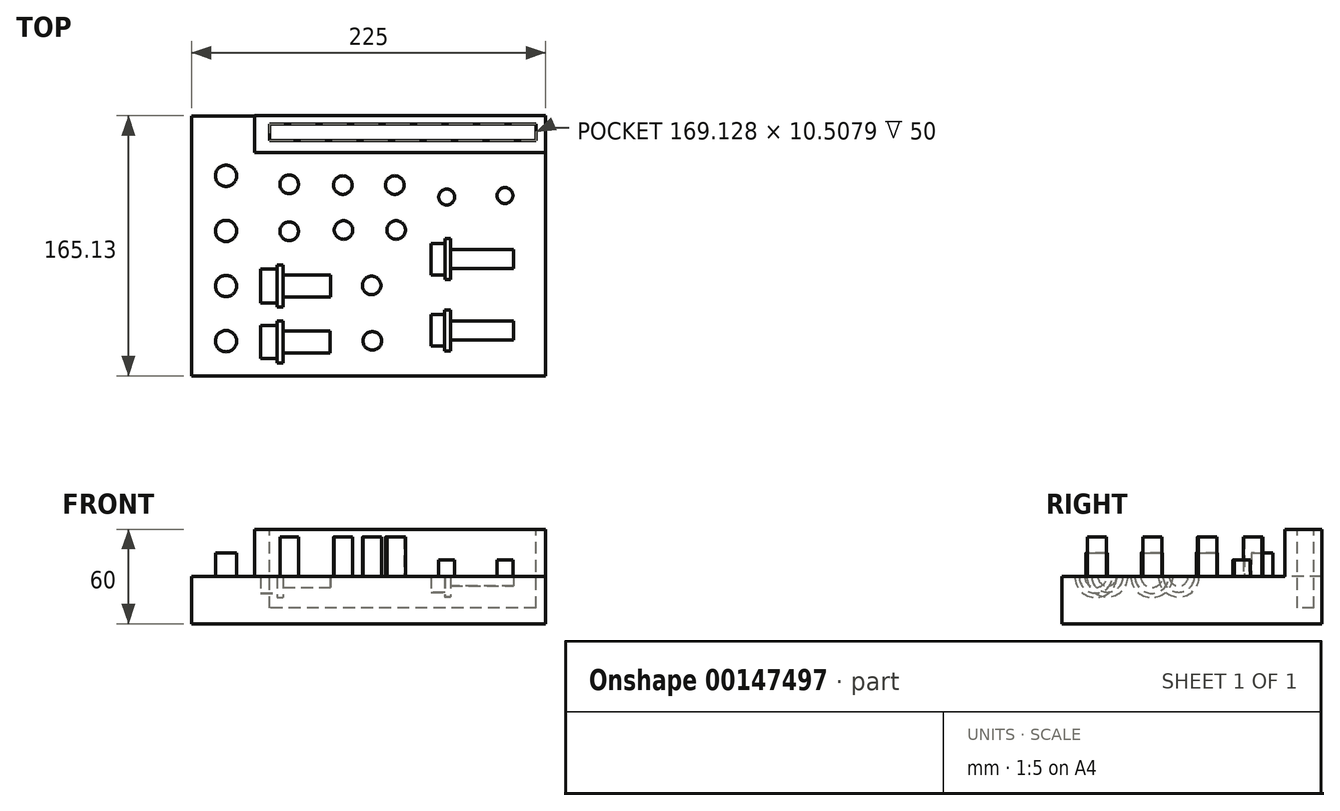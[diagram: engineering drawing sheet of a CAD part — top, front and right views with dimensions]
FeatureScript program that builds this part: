
annotation { "Feature Type Name" : "Feature", "Feature Type Description" : "" }
export const myFeature = defineFeature(function(context is Context, id is Id, definition is map)
    precondition{}
    {
        {
            var Q0;
            Q0=qCreatedBy(makeId("Top.planeOp"),FACE);
            var sketch = newSketch(context, id + "F0", { "sketchPlane" : qUnion([Q0])});
            skLineSegment(sketch, "E0.bottom", {"start": v(0, 0) * mm, "end": v(225, 0) * mm});
            skLineSegment(sketch, "E0.top", {"start": v(0, 165) * mm, "end": v(225, 165) * mm});
            skLineSegment(sketch, "E0.left", {"start": v(0, 0) * mm, "end": v(0, 165) * mm});
            skLineSegment(sketch, "E0.right", {"start": v(225, 0) * mm, "end": v(225, 165) * mm});
            skSolve(sketch);
        }
        {
            var Q0;
            Q0=makeQuery(id+"F0.imprint","IMPRINT",FACE,{"disambiguationData":[TD([[makeQuery(id+"F0.imprint","IMPRINT",EDGE,{"derivedFrom":sQuery(id+"F0.wireOp",EDGE,"E0.bottom")}),1.0]])]});
            extrude(context, id + "F1", {"entities" : qUnion([Q0]), "depth" : 30 * mm});
        }
        {
            var Q0;
            Q0=makeQuery(id+"F1.opExtrude","CAP_FACE",FACE,{"disambiguationData":[OSD([sQuery(id+"F0.wireOp",EDGE,"E0.bottom"),sQuery(id+"F0.wireOp",EDGE,"E0.top"),sQuery(id+"F0.wireOp",EDGE,"E0.left"),sQuery(id+"F0.wireOp",EDGE,"E0.right")])],"isStart":false});
            var sketch = newSketch(context, id + "F2", { "sketchPlane" : qUnion([Q0])});
            skLineSegment(sketch, "E1", {"start": v(0, 0) * mm, "end": v(22, 0) * mm, "construction": true});
            skLineSegment(sketch, "E2", {"start": v(22, 0) * mm, "end": v(22, 22) * mm, "construction": true});
            skLineSegment(sketch, "E3", {"start": v(22, 22) * mm, "end": v(22, 57) * mm, "construction": true});
            skLineSegment(sketch, "E4", {"start": v(22, 57) * mm, "end": v(22, 92) * mm, "construction": true});
            skLineSegment(sketch, "E5", {"start": v(22, 92) * mm, "end": v(22, 127) * mm, "construction": true});
            skCircle(sketch, "E6", {"center": v(22, 127) * mm, "radius": 6.75 * mm});
            skCircle(sketch, "E7", {"center": v(22, 92) * mm, "radius": 6.75 * mm});
            skCircle(sketch, "E8", {"center": v(22, 57) * mm, "radius": 6.75 * mm});
            skCircle(sketch, "E9", {"center": v(22, 22) * mm, "radius": 6.75 * mm});
            skSolve(sketch);
        }
        {
            var Q0;
            Q0=makeQuery(id+"F2.imprint","IMPRINT",FACE,{"disambiguationData":[TD([[makeQuery(id+"F2.imprint","IMPRINT",EDGE,{"derivedFrom":sQuery(id+"F2.wireOp",EDGE,"E6")}),1.0]])]});
            var Q1;
            Q1=makeQuery(id+"F2.imprint","IMPRINT",FACE,{"disambiguationData":[TD([[makeQuery(id+"F2.imprint","IMPRINT",EDGE,{"derivedFrom":sQuery(id+"F2.wireOp",EDGE,"E7")}),1.0]])]});
            var Q2;
            Q2=makeQuery(id+"F2.imprint","IMPRINT",FACE,{"disambiguationData":[TD([[makeQuery(id+"F2.imprint","IMPRINT",EDGE,{"derivedFrom":sQuery(id+"F2.wireOp",EDGE,"E8")}),1.0]])]});
            var Q3;
            Q3=makeQuery(id+"F2.imprint","IMPRINT",FACE,{"disambiguationData":[TD([[makeQuery(id+"F2.imprint","IMPRINT",EDGE,{"derivedFrom":sQuery(id+"F2.wireOp",EDGE,"E9")}),1.0]])]});
            extrude(context, id + "F3", {"entities" : qUnion([Q0, Q1, Q2, Q3]), "operationType" : NewBodyOperationType.ADD, "depth" : 15 * mm});
        }
        {
            var Q0;
            Q0=makeQuery(id+"F1.opExtrude","CAP_FACE",FACE,{"disambiguationData":[OSD([sQuery(id+"F0.wireOp",EDGE,"E0.bottom"),sQuery(id+"F0.wireOp",EDGE,"E0.top"),sQuery(id+"F0.wireOp",EDGE,"E0.left"),sQuery(id+"F0.wireOp",EDGE,"E0.right")])],"isStart":false});
            var sketch = newSketch(context, id + "F4", { "sketchPlane" : qUnion([Q0])});
            skLineSegment(sketch, "E10", {"start": v(0, 0) * mm, "end": v(44, 0) * mm});
            skLineSegment(sketch, "E11", {"start": v(44, 0) * mm, "end": v(44, 22) * mm});
            skLineSegment(sketch, "E12", {"start": v(44, 22) * mm, "end": v(44, 57) * mm});
            skLineSegment(sketch, "E13.bottom", {"start": v(44, 57) * mm, "end": v(54.5, 57) * mm});
            skLineSegment(sketch, "E13.top", {"start": v(44, 46.25) * mm, "end": v(54.5, 46.25) * mm});
            skLineSegment(sketch, "E13.left", {"start": v(44, 57) * mm, "end": v(44, 46.25) * mm});
            skLineSegment(sketch, "E14.bottom", {"start": v(54.5, 57) * mm, "end": v(58.25, 57) * mm});
            skLineSegment(sketch, "E14.top", {"start": v(54.5, 43.65) * mm, "end": v(58.25, 43.65) * mm});
            skLineSegment(sketch, "E14.left", {"start": v(54.5, 46.25) * mm, "end": v(54.5, 43.65) * mm});
            skLineSegment(sketch, "E14.right", {"start": v(58.25, 50) * mm, "end": v(58.25, 43.65) * mm});
            skLineSegment(sketch, "E15.bottom", {"start": v(58.25, 57) * mm, "end": v(88.25, 57) * mm});
            skLineSegment(sketch, "E15.top", {"start": v(58.25, 50) * mm, "end": v(88.25, 50) * mm});
            skLineSegment(sketch, "E15.right", {"start": v(88.25, 57) * mm, "end": v(88.25, 50) * mm});
            skSolve(sketch);
        }
        {
            var Q0;
            {var subQ2=sQuery(id+"F4.wireOp",EDGE,"E10");Q0=makeQuery(id+"F4.imprint","IMPRINT",FACE,{"disambiguationData":[TD([[makeQuery(id+"F4.imprint","IMPRINT",EDGE,{"derivedFrom":subQ2}),1.0]])]});}
            var sketch = newSketch(context, id + "F5", { "sketchPlane" : qUnion([Q0])});
            skLineSegment(sketch, "E16.bottom", {"start": v(43.99, 21.41) * mm, "end": v(54.49, 21.41) * mm});
            skLineSegment(sketch, "E16.top", {"start": v(43.99, 10.87) * mm, "end": v(54.49, 10.87) * mm});
            skLineSegment(sketch, "E16.left", {"start": v(43.99, 21.41) * mm, "end": v(43.99, 10.87) * mm});
            skLineSegment(sketch, "E16.right", {"start": v(54.49, 21.41) * mm, "end": v(54.49, 10.87) * mm});
            skLineSegment(sketch, "E17.bottom", {"start": v(54.49, 21.41) * mm, "end": v(58.24, 21.41) * mm});
            skLineSegment(sketch, "E17.top", {"start": v(54.49, 8.06) * mm, "end": v(58.24, 8.06) * mm});
            skLineSegment(sketch, "E17.left", {"start": v(54.49, 21.41) * mm, "end": v(54.49, 8.06) * mm});
            skLineSegment(sketch, "E17.right", {"start": v(58.24, 21.41) * mm, "end": v(58.24, 8.06) * mm});
            skLineSegment(sketch, "E18.bottom", {"start": v(58.24, 21.41) * mm, "end": v(88.24, 21.41) * mm});
            skLineSegment(sketch, "E18.top", {"start": v(58.24, 14.41) * mm, "end": v(88.24, 14.41) * mm});
            skLineSegment(sketch, "E18.left", {"start": v(58.24, 21.41) * mm, "end": v(58.24, 14.41) * mm});
            skLineSegment(sketch, "E18.right", {"start": v(88.24, 21.41) * mm, "end": v(88.24, 14.41) * mm});
            skSolve(sketch);
        }
        {
            var Q0;
            {var subQ0=sQuery(id+"F5.wireOp",EDGE,"E16.bottom");Q0=makeQuery(id+"F5.imprint","IMPRINT",FACE,{"disambiguationData":[TD([[makeQuery(id+"F5.imprint","IMPRINT",EDGE,{"derivedFrom":subQ0}),-1.0]])]});}
            var Q1;
            {var subQ3=sQuery(id+"F5.wireOp",EDGE,"E17.bottom");Q1=makeQuery(id+"F5.imprint","IMPRINT",FACE,{"disambiguationData":[TD([[makeQuery(id+"F5.imprint","IMPRINT",EDGE,{"derivedFrom":subQ3}),-1.0]])]});}
            var Q2;
            Q2=makeQuery(id+"F5.imprint","IMPRINT",FACE,{"disambiguationData":[TD([[makeQuery(id+"F5.imprint","IMPRINT",EDGE,{"derivedFrom":sQuery(id+"F5.wireOp",EDGE,"E18.bottom")}),-1.0]])]});
            var Q3;
            Q3=sQuery(id+"F5.wireOp",EDGE,"E16.bottom");
            revolve(context, id + "F6", {"operationType" : NewBodyOperationType.REMOVE, "entities" : qUnion([Q0, Q1, Q2]), "axis" : qUnion([Q3]), "revolveType" : RevolveType.FULL, "oppositeDirection" : true});
        }
        {
            var Q0;
            {var subQ2=sQuery(id+"F4.wireOp",EDGE,"E10");Q0=makeQuery(id+"F4.imprint","IMPRINT",FACE,{"disambiguationData":[TD([[makeQuery(id+"F4.imprint","IMPRINT",EDGE,{"derivedFrom":subQ2}),1.0]])]});}
            var sketch = newSketch(context, id + "F7", { "sketchPlane" : qUnion([Q0])});
            skSolve(sketch);
        }
        {
            var Q0;
            Q0=makeQuery(id+"F7.imprint","IMPRINT",FACE,{"disambiguationData":[TD([[makeQuery(id+"F7.imprint","IMPRINT",EDGE,{"derivedFrom":makeQuery(id+"F4.imprint","IMPRINT",EDGE,{"derivedFrom":sQuery(id+"F4.wireOp",EDGE,"E13.bottom")})}),-1.0]])]});
            var Q1;
            Q1=sQuery(id+"F4.wireOp",EDGE,"E13.bottom");
            revolve(context, id + "F8", {"operationType" : NewBodyOperationType.REMOVE, "entities" : qUnion([Q0]), "axis" : qUnion([Q1]), "revolveType" : RevolveType.FULL, "oppositeDirection" : true});
        }
        {
            var Q0;
            Q0=makeQuery(id+"F1.opExtrude","CAP_FACE",FACE,{"disambiguationData":[OSD([sQuery(id+"F0.wireOp",EDGE,"E0.bottom"),sQuery(id+"F0.wireOp",EDGE,"E0.top"),sQuery(id+"F0.wireOp",EDGE,"E0.left"),sQuery(id+"F0.wireOp",EDGE,"E0.right")])],"isStart":false});
            var sketch = newSketch(context, id + "F9", { "sketchPlane" : qUnion([Q0])});
            skLineSegment(sketch, "E19.bottom", {"start": v(0, 0) * mm, "end": v(109.82, 0) * mm, "construction": true});
            skLineSegment(sketch, "E19.top", {"start": v(0, 27.52) * mm, "end": v(109.82, 27.52) * mm, "construction": true});
            skLineSegment(sketch, "E19.left", {"start": v(0, 0) * mm, "end": v(0, 27.52) * mm, "construction": true});
            skLineSegment(sketch, "E19.right", {"start": v(109.82, 0) * mm, "end": v(109.82, 27.52) * mm, "construction": true});
            skSolve(sketch);
        }
        {
            var Q0;
            {var subQ3=sQuery(id+"F0.wireOp",EDGE,"E0.bottom");Q0=makeQuery(id+"F9.imprint","IMPRINT",FACE,{"disambiguationData":[TD([[makeQuery(id+"F9.imprint","IMPRINT",EDGE,{"derivedFrom":makeQuery(id+"F1.opExtrude","CAP_EDGE",EDGE,{"disambiguationData":[OSD([subQ3])],"isStart":false})}),1.0]])]});}
            var sketch = newSketch(context, id + "F10", { "sketchPlane" : qUnion([Q0])});
            skLineSegment(sketch, "E20.bottom", {"start": v(0, 0) * mm, "end": v(62.12, 0) * mm, "construction": true});
            skLineSegment(sketch, "E20.top", {"start": v(0, 121.58) * mm, "end": v(62.12, 121.58) * mm, "construction": true});
            skLineSegment(sketch, "E20.left", {"start": v(0, 0) * mm, "end": v(0, 121.58) * mm, "construction": true});
            skLineSegment(sketch, "E20.right", {"start": v(62.12, 0) * mm, "end": v(62.12, 121.58) * mm, "construction": true});
            skCircle(sketch, "E21", {"center": v(62.12, 121.58) * mm, "radius": 5.9 * mm});
            skCircle(sketch, "E22", {"center": v(62.12, 91.76) * mm, "radius": 5.9 * mm});
            skCircle(sketch, "E23", {"center": v(96.63, 92.6) * mm, "radius": 5.9 * mm});
            skCircle(sketch, "E24", {"center": v(96.19, 121.12) * mm, "radius": 5.9 * mm});
            skCircle(sketch, "E25", {"center": v(114.9, 22.16) * mm, "radius": 5.9 * mm});
            skCircle(sketch, "E26", {"center": v(129.18, 121.12) * mm, "radius": 5.9 * mm});
            skCircle(sketch, "E27", {"center": v(130.07, 92.6) * mm, "radius": 5.9 * mm});
            skCircle(sketch, "E28", {"center": v(114.46, 57.37) * mm, "radius": 5.9 * mm});
            skSolve(sketch);
        }
        {
            var Q0;
            Q0=makeQuery(id+"F10.imprint","IMPRINT",FACE,{"disambiguationData":[TD([[makeQuery(id+"F10.imprint","IMPRINT",EDGE,{"derivedFrom":sQuery(id+"F10.wireOp",EDGE,"CW1vxD1U-gibG-Lz99-enL3-3w2vIjQjNwkh")}),1.0]])]});
            var Q1;
            Q1=makeQuery(id+"F10.imprint","IMPRINT",FACE,{"disambiguationData":[TD([[makeQuery(id+"F10.imprint","IMPRINT",EDGE,{"derivedFrom":sQuery(id+"F10.wireOp",EDGE,"E21")}),1.0]])]});
            var Q2;
            Q2=makeQuery(id+"F10.imprint","IMPRINT",FACE,{"disambiguationData":[TD([[makeQuery(id+"F10.imprint","IMPRINT",EDGE,{"derivedFrom":sQuery(id+"F10.wireOp",EDGE,"E22")}),1.0]])]});
            var Q3;
            Q3=sQuery(id+"F10.wireOp",EDGE,"CW1vxD1U-gibG-Lz99-enL3-3w2vIjQjNwkh");
            var Q4;
            Q4=sQuery(id+"F10.wireOp",EDGE,"E21");
            extrude(context, id + "F11", {"entities" : qUnion([Q0, Q1, Q2]), "operationType" : NewBodyOperationType.ADD, "surfaceEntities" : qUnion([Q3, Q4]), "depth" : 12.85 * mm});
        }
        {
            var Q0;
            Q0 = qSketchRegion(id + "F10", true);
            extrude(context, id + "F12", {"entities" : qUnion([Q0]), "operationType" : NewBodyOperationType.ADD, "depth" : 25 * mm});
        }
        {
            var Q0;
            {var subQ3=sQuery(id+"F0.wireOp",EDGE,"E0.bottom");Q0=makeQuery(id+"F9.imprint","IMPRINT",FACE,{"disambiguationData":[TD([[makeQuery(id+"F9.imprint","IMPRINT",EDGE,{"derivedFrom":makeQuery(id+"F1.opExtrude","CAP_EDGE",EDGE,{"disambiguationData":[OSD([subQ3])],"isStart":false})}),1.0]])]});}
            var sketch = newSketch(context, id + "F13", { "sketchPlane" : qUnion([Q0])});
            skLineSegment(sketch, "E29", {"start": v(0, 0) * mm, "end": v(152.24, 0) * mm, "construction": true});
            skLineSegment(sketch, "E30", {"start": v(152.24, 0) * mm, "end": v(152.24, 28.79) * mm, "construction": true});
            skLineSegment(sketch, "E31.bottom", {"start": v(152.24, 28.79) * mm, "end": v(160.94, 28.79) * mm});
            skLineSegment(sketch, "E31.top", {"start": v(152.24, 18.79) * mm, "end": v(160.94, 18.79) * mm});
            skLineSegment(sketch, "E31.left", {"start": v(152.24, 28.79) * mm, "end": v(152.24, 18.79) * mm});
            skLineSegment(sketch, "E32.bottom", {"start": v(160.94, 28.79) * mm, "end": v(164.7, 28.79) * mm});
            skLineSegment(sketch, "E32.top", {"start": v(160.94, 15.79) * mm, "end": v(164.7, 15.79) * mm});
            skLineSegment(sketch, "E32.left", {"start": v(160.94, 18.79) * mm, "end": v(160.94, 15.79) * mm});
            skLineSegment(sketch, "E32.right", {"start": v(164.7, 22.79) * mm, "end": v(164.7, 15.79) * mm});
            skLineSegment(sketch, "E33.bottom", {"start": v(164.7, 28.79) * mm, "end": v(204.7, 28.79) * mm});
            skLineSegment(sketch, "E33.top", {"start": v(164.7, 22.79) * mm, "end": v(204.7, 22.79) * mm});
            skLineSegment(sketch, "E33.right", {"start": v(204.7, 28.79) * mm, "end": v(204.7, 22.79) * mm});
            skSolve(sketch);
        }
        {
            var Q0;
            Q0 = qSketchRegion(id + "F13", true);
            var Q1;
            Q1=sQuery(id+"F13.wireOp",EDGE,"E33.bottom");
            revolve(context, id + "F14", {"operationType" : NewBodyOperationType.REMOVE, "entities" : qUnion([Q0]), "axis" : qUnion([Q1]), "revolveType" : RevolveType.FULL, "oppositeDirection" : true});
        }
        {
            var Q0;
            {var subQ3=sQuery(id+"F0.wireOp",EDGE,"E0.bottom");Q0=makeQuery(id+"F9.imprint","IMPRINT",FACE,{"disambiguationData":[TD([[makeQuery(id+"F9.imprint","IMPRINT",EDGE,{"derivedFrom":makeQuery(id+"F1.opExtrude","CAP_EDGE",EDGE,{"disambiguationData":[OSD([subQ3])],"isStart":false})}),1.0]])]});}
            var sketch = newSketch(context, id + "F15", { "sketchPlane" : qUnion([Q0])});
            skLineSegment(sketch, "E34", {"start": v(152.27, 42.55) * mm, "end": v(152.27, 74.12) * mm, "construction": true});
            skLineSegment(sketch, "E35.bottom", {"start": v(152.27, 74.12) * mm, "end": v(160.97, 74.12) * mm});
            skLineSegment(sketch, "E35.top", {"start": v(152.27, 64.12) * mm, "end": v(160.97, 64.12) * mm});
            skLineSegment(sketch, "E35.left", {"start": v(152.27, 74.12) * mm, "end": v(152.27, 64.12) * mm});
            skLineSegment(sketch, "E35.right", {"start": v(160.97, 74.12) * mm, "end": v(160.97, 64.12) * mm});
            skLineSegment(sketch, "E36.bottom", {"start": v(160.97, 74.12) * mm, "end": v(164.72, 74.12) * mm});
            skLineSegment(sketch, "E36.top", {"start": v(160.97, 61.12) * mm, "end": v(164.72, 61.12) * mm});
            skLineSegment(sketch, "E36.left", {"start": v(160.97, 74.12) * mm, "end": v(160.97, 61.12) * mm});
            skLineSegment(sketch, "E36.right", {"start": v(164.72, 74.12) * mm, "end": v(164.72, 61.12) * mm});
            skLineSegment(sketch, "E37.bottom", {"start": v(164.72, 74.12) * mm, "end": v(204.72, 74.12) * mm});
            skLineSegment(sketch, "E37.top", {"start": v(164.72, 68.12) * mm, "end": v(204.72, 68.12) * mm});
            skLineSegment(sketch, "E37.left", {"start": v(164.72, 74.12) * mm, "end": v(164.72, 68.12) * mm});
            skLineSegment(sketch, "E37.right", {"start": v(204.72, 74.12) * mm, "end": v(204.72, 68.12) * mm});
            skSolve(sketch);
        }
        {
            var Q0;
            Q0 = qSketchRegion(id + "F15", true);
            var Q1;
            Q1=sQuery(id+"F15.wireOp",EDGE,"E37.bottom");
            revolve(context, id + "F16", {"operationType" : NewBodyOperationType.REMOVE, "entities" : qUnion([Q0]), "axis" : qUnion([Q1]), "revolveType" : RevolveType.FULL});
        }
        {
            var Q0;
            {var subQ3=sQuery(id+"F0.wireOp",EDGE,"E0.bottom");Q0=makeQuery(id+"F9.imprint","IMPRINT",FACE,{"disambiguationData":[TD([[makeQuery(id+"F9.imprint","IMPRINT",EDGE,{"derivedFrom":makeQuery(id+"F1.opExtrude","CAP_EDGE",EDGE,{"disambiguationData":[OSD([subQ3])],"isStart":false})}),1.0]])]});}
            var sketch = newSketch(context, id + "F17", { "sketchPlane" : qUnion([Q0])});
            skLineSegment(sketch, "E38", {"start": v(0, 0) * mm, "end": v(195.88, 0) * mm, "construction": true});
            skLineSegment(sketch, "E39", {"start": v(0, 0) * mm, "end": v(193.46, 0) * mm});
            skCircle(sketch, "E40", {"center": v(162.16, 113.54) * mm, "radius": 5.05 * mm});
            skCircle(sketch, "E41", {"center": v(199.16, 114.43) * mm, "radius": 5.05 * mm});
            skSolve(sketch);
        }
        {
            var Q0;
            Q0 = qSketchRegion(id + "F17", true);
            extrude(context, id + "F18", {"entities" : qUnion([Q0]), "operationType" : NewBodyOperationType.ADD, "depth" : 10.6 * mm});
        }
        {
            var Q0;
            {var subQ3=sQuery(id+"F0.wireOp",EDGE,"E0.bottom");Q0=makeQuery(id+"F9.imprint","IMPRINT",FACE,{"disambiguationData":[TD([[makeQuery(id+"F9.imprint","IMPRINT",EDGE,{"derivedFrom":makeQuery(id+"F1.opExtrude","CAP_EDGE",EDGE,{"disambiguationData":[OSD([subQ3])],"isStart":false})}),1.0]])]});}
            var sketch = newSketch(context, id + "F19", { "sketchPlane" : qUnion([Q0])});
            skLineSegment(sketch, "E42.bottom", {"start": v(40.22, 165.13) * mm, "end": v(225, 165.13) * mm});
            skLineSegment(sketch, "E42.top", {"start": v(40.22, 141.63) * mm, "end": v(225, 141.63) * mm});
            skLineSegment(sketch, "E42.left", {"start": v(40.22, 165.13) * mm, "end": v(40.22, 141.63) * mm});
            skLineSegment(sketch, "E42.right", {"start": v(225, 165.13) * mm, "end": v(225, 141.63) * mm});
            skSolve(sketch);
        }
        {
            var Q0;
            Q0 = qSketchRegion(id + "F19", true);
            extrude(context, id + "F20", {"entities" : qUnion([Q0]), "operationType" : NewBodyOperationType.ADD, "depth" : 30 * mm});
        }
        {
            var Q0;
            Q0=makeQuery(id+"F20.opExtrude","CAP_FACE",FACE,{"disambiguationData":[OSD([sQuery(id+"F19.wireOp",EDGE,"E42.bottom"),sQuery(id+"F19.wireOp",EDGE,"E42.top"),sQuery(id+"F19.wireOp",EDGE,"E42.left"),sQuery(id+"F19.wireOp",EDGE,"E42.right")])],"isStart":false});
            var sketch = newSketch(context, id + "F21", { "sketchPlane" : qUnion([Q0])});
            skLineSegment(sketch, "E43.bottom", {"start": v(218.83, 160) * mm, "end": v(49.7, 160) * mm});
            skLineSegment(sketch, "E43.top", {"start": v(218.83, 149.49) * mm, "end": v(49.7, 149.49) * mm});
            skLineSegment(sketch, "E43.left", {"start": v(218.83, 160) * mm, "end": v(218.83, 149.49) * mm});
            skLineSegment(sketch, "E43.right", {"start": v(49.7, 160) * mm, "end": v(49.7, 149.49) * mm});
            skSolve(sketch);
        }
        {
            var Q0;
            Q0 = qSketchRegion(id + "F21", true);
            extrude(context, id + "F22", {"entities" : qUnion([Q0]), "operationType" : NewBodyOperationType.REMOVE, "oppositeDirection" : true, "depth" : 50 * mm});
        }
    });
